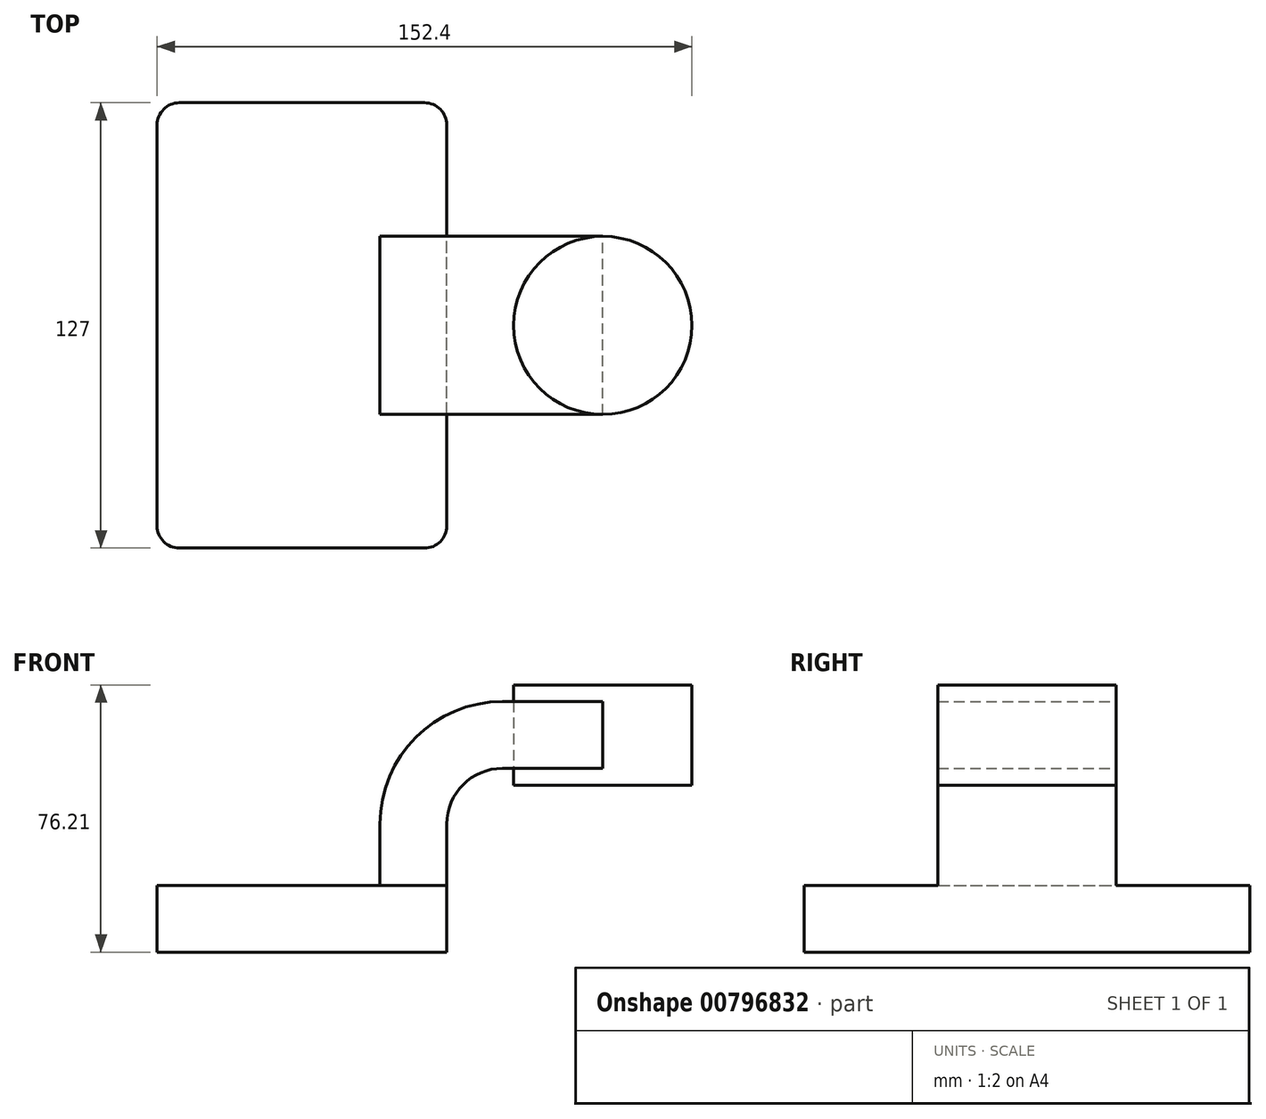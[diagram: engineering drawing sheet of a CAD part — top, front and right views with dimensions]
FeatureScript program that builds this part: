
annotation { "Feature Type Name" : "Feature", "Feature Type Description" : "" }
export const myFeature = defineFeature(function(context is Context, id is Id, definition is map)
    precondition{}
    {
        {
            var Q0;
            Q0=qCreatedBy(makeId("Front.planeOp"),FACE);
            var sketch = newSketch(context, id + "F0", { "sketchPlane" : qUnion([Q0])});
            skLineSegment(sketch, "E0.bottom", {"start": v(-41.28, 9.52) * mm, "end": v(41.27, 9.53) * mm});
            skLineSegment(sketch, "E0.top", {"start": v(-41.28, -9.52) * mm, "end": v(41.28, -9.52) * mm});
            skLineSegment(sketch, "E0.left", {"start": v(-41.28, 9.52) * mm, "end": v(-41.28, -9.53) * mm});
            skLineSegment(sketch, "E0.right", {"start": v(41.27, 9.53) * mm, "end": v(41.28, -9.52) * mm});
            skPoint(sketch, "E0.middle", {"position": v(0, 0) * mm});
            skLineSegment(sketch, "E1.bottom", {"start": v(60.33, 38.1) * mm, "end": v(111.13, 38.1) * mm});
            skLineSegment(sketch, "E1.top", {"start": v(60.32, 66.68) * mm, "end": v(111.12, 66.68) * mm});
            skLineSegment(sketch, "E1.left", {"start": v(60.33, 38.1) * mm, "end": v(60.33, 66.68) * mm});
            skLineSegment(sketch, "E1.right", {"start": v(111.13, 38.1) * mm, "end": v(111.12, 66.68) * mm});
            skPoint(sketch, "E1.middle", {"position": v(85.73, 52.39) * mm});
            skLineSegment(sketch, "E2", {"start": v(41.27, 9.53) * mm, "end": v(41.27, 27) * mm});
            skArc(sketch, "E3", {"start": v(41.27, 27) * mm, "mid": v(45.92, 38.23) * mm, "end": v(57.15, 42.88) * mm});
            skLineSegment(sketch, "E4", {"start": v(57.15, 42.88) * mm, "end": v(85.72, 42.88) * mm});
            skLineSegment(sketch, "E5.0", {"start": v(57.15, 61.93) * mm, "end": v(85.72, 61.93) * mm});
            skArc(sketch, "E5.1", {"start": v(22.22, 27) * mm, "mid": v(32.45, 51.7) * mm, "end": v(57.15, 61.93) * mm});
            skLineSegment(sketch, "E5.2", {"start": v(22.22, 9.53) * mm, "end": v(22.22, 27) * mm});
            skLineSegment(sketch, "E6", {"start": v(85.72, 38.1) * mm, "end": v(85.72, 66.68) * mm});
            skFitSpline(sketch, "E7", {"points": [v(-41.28, 9.53) * mm, v(57.15, 61.93) * mm], "startDerivative": vector(6.6, 119.58) * mm, "endDerivative": vector(160.66, -2.65) * mm});
            skSolve(sketch);
        }
        {
            var Q0;
            Q0=makeQuery(id+"F0.imprint","IMPRINT",FACE,{"disambiguationData":[TD([[makeQuery(id+"F0.imprint","IMPRINT",EDGE,{"derivedFrom":sQuery(id+"F0.wireOp",EDGE,"E0.top")}),1.0]])]});
            extrude(context, id + "F1", {"entities" : qUnion([Q0]), "endBound" : BoundingType.SYMMETRIC, "depth" : 127 * mm, "offsetDistance" : 25.4 * mm});
        }
        {
            var Q0;
            {var subQ1=sQuery(id+"F0.wireOp",EDGE,"E2");Q0=makeQuery(id+"F0.imprint","IMPRINT",FACE,{"disambiguationData":[TD([[makeQuery(id+"F0.imprint","IMPRINT",EDGE,{"derivedFrom":subQ1}),1.0]])]});}
            var Q1;
            {var subQ0=sQuery(id+"F0.wireOp",EDGE,"E4");var subQ1=sQuery(id+"F0.wireOp",EDGE,"E1.left");var subQ2=makeQuery(id+"F0.imprint","INTERSECT",VERTEX,{"derivedFrom":[subQ1,subQ0]});Q1=makeQuery(id+"F0.imprint","IMPRINT",FACE,{"disambiguationData":[TD([[makeQuery(id+"F0.imprint","IMPRINT",EDGE,{"disambiguationData":[TD([[subQ2,-1.0]])],"derivedFrom":subQ1}),-1.0]])]});}
            extrude(context, id + "F2", {"entities" : qUnion([Q0, Q1]), "operationType" : NewBodyOperationType.ADD, "endBound" : BoundingType.SYMMETRIC, "depth" : 50.8 * mm, "offsetDistance" : 25.4 * mm});
        }
        {
            var Q0;
            Q0=makeQuery(id+"F0.imprint","IMPRINT",FACE,{"disambiguationData":[TD([[makeQuery(id+"F0.imprint","IMPRINT",EDGE,{"derivedFrom":sQuery(id+"F0.wireOp",EDGE,"E5.1")}),1.0]])]});
            extrude(context, id + "F3", {"entities" : qUnion([Q0]), "operationType" : NewBodyOperationType.ADD, "endBound" : BoundingType.SYMMETRIC, "depth" : 15.88 * mm, "offsetDistance" : 25.4 * mm});
        }
        {
            var Q0;
            {var subQ0=sQuery(id+"F0.wireOp",EDGE,"E1.right");Q0=makeQuery(id+"F0.imprint","IMPRINT",FACE,{"disambiguationData":[TD([[makeQuery(id+"F0.imprint","IMPRINT",EDGE,{"derivedFrom":subQ0}),1.0]])]});}
            var Q1;
            Q1=sQuery(id+"F0.wireOp",EDGE,"E6");
            revolve(context, id + "F4", {"surfaceOperationType" : NewSurfaceOperationType.NEW, "entities" : qUnion([Q0]), "axis" : qUnion([Q1]), "revolveType" : RevolveType.FULL});
        }
        {
            var Q0;
            Q0=makeQuery(id+"F1.opExtrude","CAP_EDGE",EDGE,{"disambiguationData":[OSD([sQuery(id+"F0.wireOp",EDGE,"E0.right")])],"isStart":false});
            var Q1;
            Q1=makeQuery(id+"F1.opExtrude","CAP_EDGE",EDGE,{"disambiguationData":[OSD([sQuery(id+"F0.wireOp",EDGE,"E0.left")])],"isStart":false});
            var Q2;
            Q2=makeQuery(id+"F1.opExtrude","CAP_EDGE",EDGE,{"disambiguationData":[OSD([sQuery(id+"F0.wireOp",EDGE,"E0.right")])],"isStart":true});
            var Q3;
            Q3=makeQuery(id+"F1.opExtrude","CAP_EDGE",EDGE,{"disambiguationData":[OSD([sQuery(id+"F0.wireOp",EDGE,"E0.left")])],"isStart":true});
            fillet(context, id + "F5", {"entities" : qUnion([Q0, Q1, Q2, Q3]), "radius" : 6.35 * mm, "tangentPropagation" : true, "allowEdgeOverflow" : false});
        }
    });
